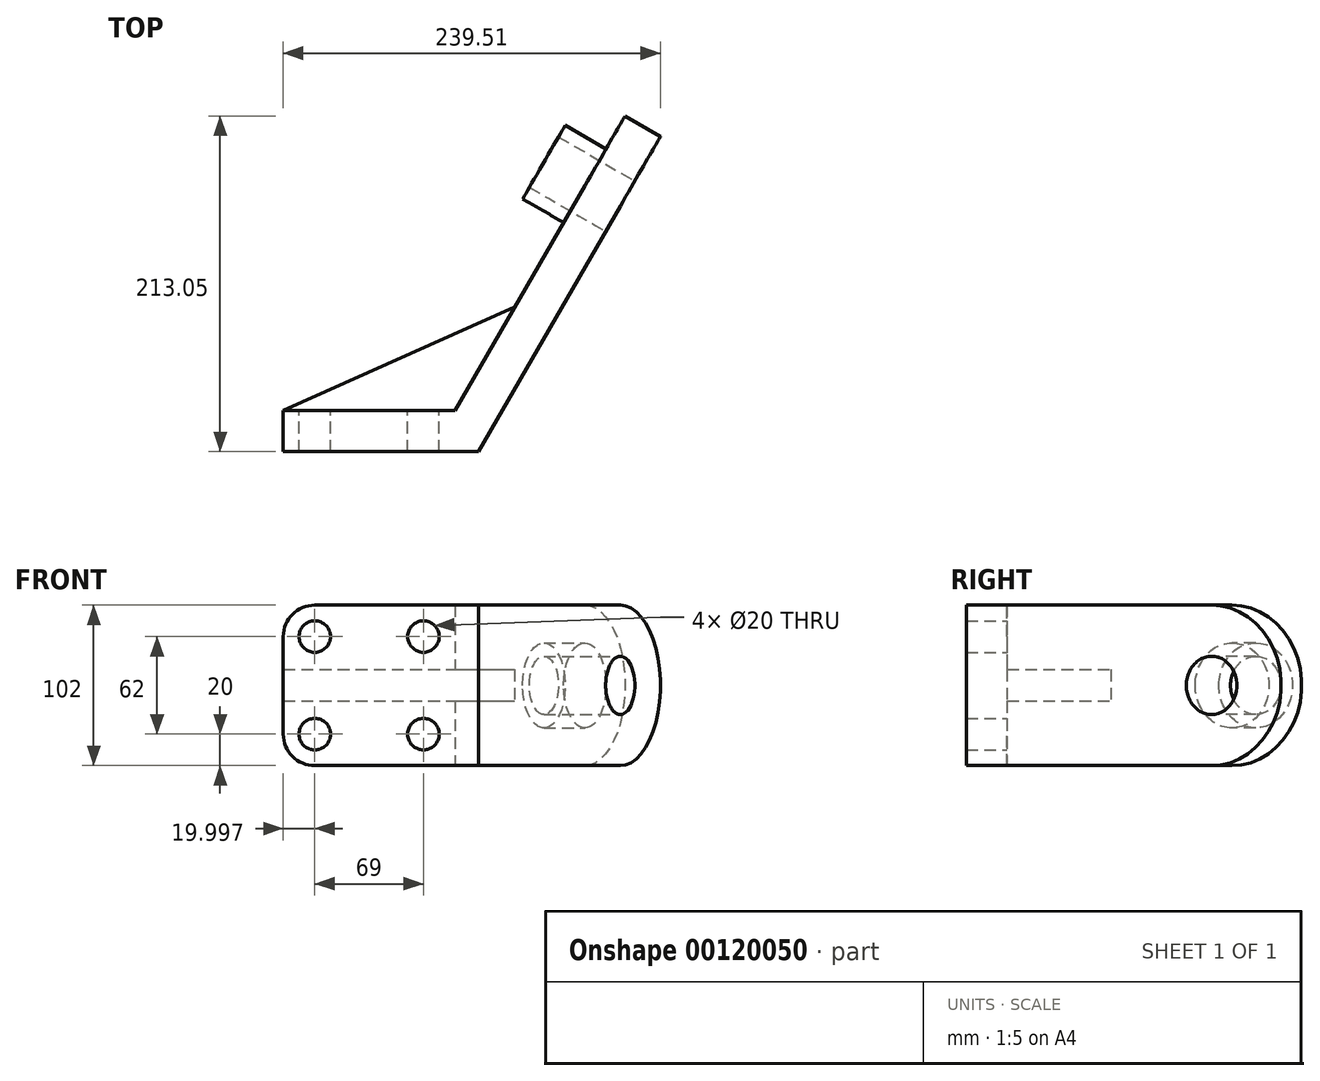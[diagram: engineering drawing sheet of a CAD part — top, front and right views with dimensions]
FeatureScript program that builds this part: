
annotation { "Feature Type Name" : "Feature", "Feature Type Description" : "" }
export const myFeature = defineFeature(function(context is Context, id is Id, definition is map)
    precondition{}
    {
        {
            var Q0;
            Q0=qCreatedBy(makeId("Top.planeOp"),FACE);
            var sketch = newSketch(context, id + "F0", { "sketchPlane" : qUnion([Q0])});
            skLineSegment(sketch, "E0", {"start": v(-50.24, -12.87) * mm, "end": v(73.77, -12.87) * mm});
            skLineSegment(sketch, "E1", {"start": v(-50.24, -12.87) * mm, "end": v(-50.24, 13.13) * mm});
            skLineSegment(sketch, "E2", {"start": v(-50.24, 13.13) * mm, "end": v(58.76, 13.13) * mm});
            skLineSegment(sketch, "E3", {"start": v(58.76, 13.13) * mm, "end": v(166.75, 200.18) * mm});
            skLineSegment(sketch, "E4", {"start": v(166.75, 200.18) * mm, "end": v(189.27, 187.18) * mm});
            skLineSegment(sketch, "E5", {"start": v(73.77, -12.87) * mm, "end": v(189.27, 187.18) * mm});
            skSolve(sketch);
        }
        {
            var Q0;
            Q0 = qSketchRegion(id + "F0", true);
            extrude(context, id + "F1", {"entities" : qUnion([Q0]), "depth" : 102 * mm});
        }
        {
            var Q0;
            Q0=makeQuery(id+"F1.opExtrude","CAP_EDGE",EDGE,{"disambiguationData":[OSD([sQuery(id+"F0.wireOp",EDGE,"E4")])],"isStart":true});
            var Q1;
            Q1=makeQuery(id+"F1.opExtrude","CAP_EDGE",EDGE,{"disambiguationData":[OSD([sQuery(id+"F0.wireOp",EDGE,"E4")])],"isStart":false});
            fillet(context, id + "F2", {"entities" : qUnion([Q0, Q1]), "radius" : 51 * mm, "tangentPropagation" : true, "allowEdgeOverflow" : false});
        }
        {
            var Q0;
            Q0=makeQuery(id+"F1.opExtrude","SWEPT_FACE",FACE,{"disambiguationData":[OSD([sQuery(id+"F0.wireOp",EDGE,"E3")])]});
            var sketch = newSketch(context, id + "F3", { "sketchPlane" : qUnion([Q0])});
            skLineSegment(sketch, "E6", {"start": v(-205.73, 0) * mm, "end": v(-205.73, 102) * mm, "construction": true});
            skCircle(sketch, "E7", {"center": v(-205.73, 51) * mm, "radius": 27 * mm});
            skCircle(sketch, "E8", {"center": v(-205.73, 51) * mm, "radius": 18.5 * mm});
            skSolve(sketch);
        }
        {
            var Q0;
            Q0 = qSketchRegion(id + "F3", true);
            extrude(context, id + "F4", {"entities" : qUnion([Q0]), "operationType" : NewBodyOperationType.ADD, "depth" : 30 * mm});
        }
        {
            var Q0;
            Q0=makeQuery(id+"F1.opExtrude","CAP_FACE",FACE,{"disambiguationData":[OSD([sQuery(id+"F0.wireOp",EDGE,"E0"),sQuery(id+"F0.wireOp",EDGE,"E1"),sQuery(id+"F0.wireOp",EDGE,"E2"),sQuery(id+"F0.wireOp",EDGE,"E3"),sQuery(id+"F0.wireOp",EDGE,"E4"),sQuery(id+"F0.wireOp",EDGE,"E5")])],"isStart":false});
            cPlane(context, id + "F5", {"entities" : qUnion([Q0]), "cplaneType" : CPlaneType.OFFSET, "offset" : 51 * mm, "oppositeDirection" : true, "width" : 150 * mm, "height" : 150 * mm});
        }
        {
            var Q0;
            Q0=qCreatedBy(id+"F5.planeOp",FACE);
            var sketch = newSketch(context, id + "F6", { "sketchPlane" : qUnion([Q0])});
            skLineSegment(sketch, "E9.0", {"start": v(-50.24, 13.13) * mm, "end": v(58.76, 13.13) * mm});
            skLineSegment(sketch, "E9.1", {"start": v(58.76, 13.13) * mm, "end": v(141.25, 156) * mm});
            skLineSegment(sketch, "E10", {"start": v(-50.24, 13.13) * mm, "end": v(96.76, 78.94) * mm});
            skSolve(sketch);
        }
        {
            var Q0;
            Q0 = qSketchRegion(id + "F6", true);
            extrude(context, id + "F7", {"entities" : qUnion([Q0]), "operationType" : NewBodyOperationType.ADD, "endBound" : BoundingType.SYMMETRIC, "depth" : 20 * mm});
        }
        {
            var Q0;
            Q0=makeQuery(id+"F4.boolean.opBoolean","SPLIT",FACE,{"disambiguationData":[TD([makeQuery(id+"F4.opExtrude","SWEPT_FACE",FACE,{"disambiguationData":[OSD([sQuery(id+"F3.wireOp",EDGE,"E8")])]})])],"derivedFrom":makeQuery(id+"F1.opExtrude","SWEPT_FACE",FACE,{"disambiguationData":[OSD([sQuery(id+"F0.wireOp",EDGE,"E3")])]})});
            var sketch = newSketch(context, id + "F8", { "sketchPlane" : qUnion([Q0])});
            skCircle(sketch, "E11.0", {"center": v(-205.73, 51) * mm, "radius": 18.5 * mm});
            skSolve(sketch);
        }
        {
            var Q0;
            Q0 = qSketchRegion(id + "F8", true);
            extrude(context, id + "F9", {"entities" : qUnion([Q0]), "operationType" : NewBodyOperationType.REMOVE, "oppositeDirection" : true, "depth" : 26 * mm});
        }
        {
            var Q0;
            Q0=makeQuery(id+"F1.opExtrude","CAP_EDGE",EDGE,{"disambiguationData":[OSD([sQuery(id+"F0.wireOp",EDGE,"E1")])],"isStart":true});
            var Q1;
            Q1=makeQuery(id+"F1.opExtrude","CAP_EDGE",EDGE,{"disambiguationData":[OSD([sQuery(id+"F0.wireOp",EDGE,"E1")])],"isStart":false});
            fillet(context, id + "F10", {"entities" : qUnion([Q0, Q1]), "radius" : 20 * mm, "tangentPropagation" : true, "allowEdgeOverflow" : false});
        }
        {
            var Q0;
            {var subQ1=sQuery(id+"F6.wireOp",EDGE,"E10");var subQ3=sQuery(id+"F0.wireOp",EDGE,"E2");Q0=makeQuery(id+"F7.boolean.opBoolean","SPLIT",FACE,{"disambiguationData":[TD([makeQuery(id+"F7.opExtrude","CAP_FACE",FACE,{"disambiguationData":[OSD([sQuery(id+"F6.wireOp",EDGE,"E9.0"),sQuery(id+"F6.wireOp",EDGE,"E9.1"),subQ1])],"isStart":true})])],"derivedFrom":makeQuery(id+"F1.opExtrude","SWEPT_FACE",FACE,{"disambiguationData":[OSD([subQ3])]})});}
            var sketch = newSketch(context, id + "F11", { "sketchPlane" : qUnion([Q0])});
            skCircle(sketch, "E12", {"center": v(30.24, 20) * mm, "radius": 10 * mm});
            skCircle(sketch, "E13.0.1.0", {"center": v(30.24, 82) * mm, "radius": 10 * mm});
            skCircle(sketch, "E13.1.0.0", {"center": v(-38.76, 20) * mm, "radius": 10 * mm});
            skCircle(sketch, "E13.1.1.0", {"center": v(-38.76, 82) * mm, "radius": 10 * mm});
            skLineSegment(sketch, "E13.direction1", {"start": v(30.24, 20) * mm, "end": v(-38.76, 20) * mm, "construction": true});
            skLineSegment(sketch, "E13.direction2", {"start": v(30.24, 20) * mm, "end": v(30.24, 82) * mm, "construction": true});
            skSolve(sketch);
        }
        {
            var Q0;
            Q0 = qSketchRegion(id + "F11", true);
            extrude(context, id + "F12", {"entities" : qUnion([Q0]), "operationType" : NewBodyOperationType.REMOVE, "oppositeDirection" : true, "depth" : 26 * mm});
        }
    });
